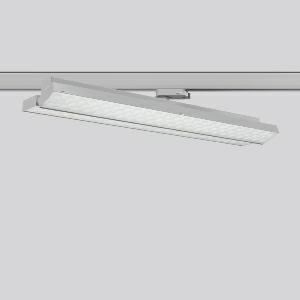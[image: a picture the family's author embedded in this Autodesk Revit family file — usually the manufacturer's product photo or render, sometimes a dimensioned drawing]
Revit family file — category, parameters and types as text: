
# Revit family: tx-move_742162_004_76_7ef8
name_source: partatom
category: Lighting Fixtures
units: mm (PartAtom-declared; Revit-internal decimal feet)

## family parameters
Cut with Voids When Loaded = No
Host = Face
Light Source = No
Part Type = Normal
Room Calculation Point = No
Round Connector Dimension = Use Diameter
Shared = No

## types (1)
- MultiLumen 1 (1 x LED Modul 830, 2925 lm, 3000)
    Apparent Load = 41 VA
    CIE Flux Codes = 77 96 99 100 100
    Color Rendering = 80
    Color Temperature = 3000
    Default Elevation = 1800 mm
    Description = Series: TX-MOVE
Multifunctional surface-mounted spotlight for area lighting. Very flat design. Housing: sheet steel, powder-coated. Rotation range: 356°. Swivel range: 90°. Consistent alignment possible with visible tilt scale. High-efficiency LED units with optimum light control thanks to clear plastic (PC) lens optics. Spezielle Mikrostrukturen reduzieren Gelbsaum. Symmetrical light distribution. With adapter for RZB 3-circuit DALI tracks. Suitable for Track on ceiling. MultiLumen: Luminous flux adjustable in 3 steps. Factory setting is the highest luminous flux. Environmentally friendly and resource-saving due to replaceable and recyclable components. 
Colour: silver, matt (approx. RAL 9006)
Length: 570 mm
Width: 119 mm
Height: 88 mm
Lamp: LED
Socket: without socket
Colour temperature: 3000K
Colour rendering index (CRI): 80
System power: 41 W
Rated luminous flux: 5850 lm
Luminous efficiency: 143 lm/W
System power 2: 57 W
Rated luminous flux 2: 7950 lm
Luminous efficiency 2: 139 lm/W
System power 3: 73 W
Rated luminous flux 3: 9700 lm
Luminous efficiency 3: 133 lm/W
Control gear: Dimmable EVG, DALI
Protection class: I
Type of protection: IP 20
    Height = 75 mm
    Lamp = 1 x LED Modul 830
    Lamp Light Flux = 2925 lm
    Lamp count = 1
    Length = 569 mm
    Lifetime = 50000 h
    Luminous efficacy = 143 lm/W
    Manufacturer = RZB
    ModVariant = No
    Model = 742162.004.76
    Mounting Place = Ceiling
    Mounting Type = Surface mounted
    Number of Poles = 1
    OnlyDefault = Yes
    Power Factor = 1
    Product Name = TX-MOVE
    Product group = Track mounted projectors
    ProductGroupID = 301
    Protection Class = Protection class I
    Protection Degree = IP 20
    RLX_Detail_Level = 1
    RLX_Emergency_Light_Flux = 0 lm
    RLX_Emergency_Type = 0
    RLX_Emergency_Type_DB = No
    RlxData = <blob elided: 33145 chars, md5=a65c7bda>
    Socket = socket
    Standby Power = 0 W
    System Light Flux = 5850 lm
    System Power = 41 W
    Type Comments = MultiLumen 1
    Type Image = 742162.004.jpg
    URL = http://relux.com
    VarID = multilumen_1
    Voltage = 0 V
    Weight = 0.00 kg
    Width = 119 mm

## geometry (parser evidence)
native form markers: Blend x4, Sweep x16
no freeform markers — native parametric forms only
